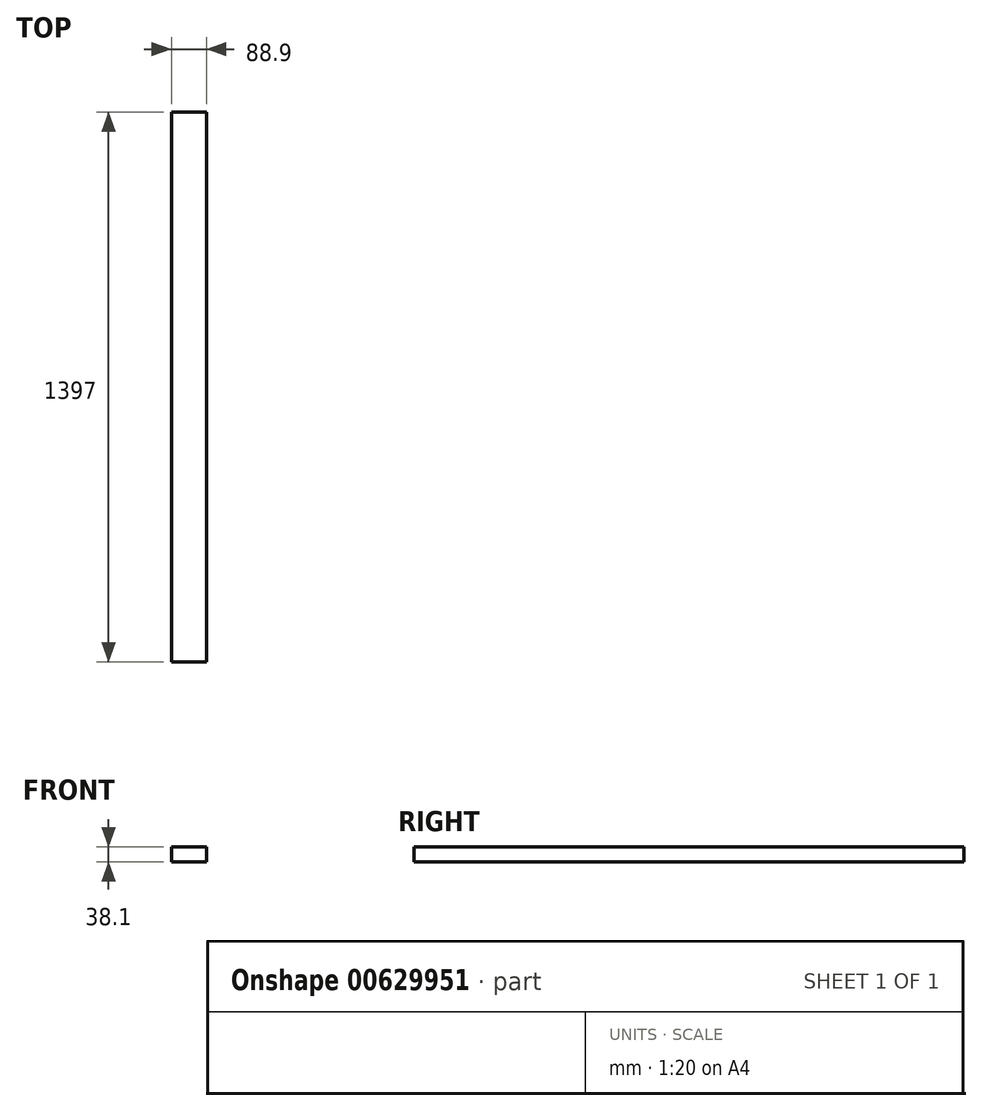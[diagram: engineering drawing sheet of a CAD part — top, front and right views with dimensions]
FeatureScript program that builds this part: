
annotation { "Feature Type Name" : "Feature", "Feature Type Description" : "" }
export const myFeature = defineFeature(function(context is Context, id is Id, definition is map)
    precondition{}
    {
        {
            var Q0;
            Q0=qCreatedBy(makeId("Front.planeOp"),FACE);
            var sketch = newSketch(context, id + "F0", { "sketchPlane" : qUnion([Q0])});
            skLineSegment(sketch, "E0.bottom", {"start": v(-40.01, 21.32) * mm, "end": v(48.89, 21.32) * mm});
            skLineSegment(sketch, "E0.top", {"start": v(-40.01, -16.78) * mm, "end": v(48.89, -16.78) * mm});
            skLineSegment(sketch, "E0.left", {"start": v(-40.01, 21.32) * mm, "end": v(-40.01, -16.78) * mm});
            skLineSegment(sketch, "E0.right", {"start": v(48.89, 21.32) * mm, "end": v(48.89, -16.78) * mm});
            skSolve(sketch);
        }
        {
            var Q0;
            Q0 = qSketchRegion(id + "F0", true);
            extrude(context, id + "F1", {"entities" : qUnion([Q0]), "depth" : 1397 * mm, "offsetDistance" : 25.4 * mm});
        }
    });
